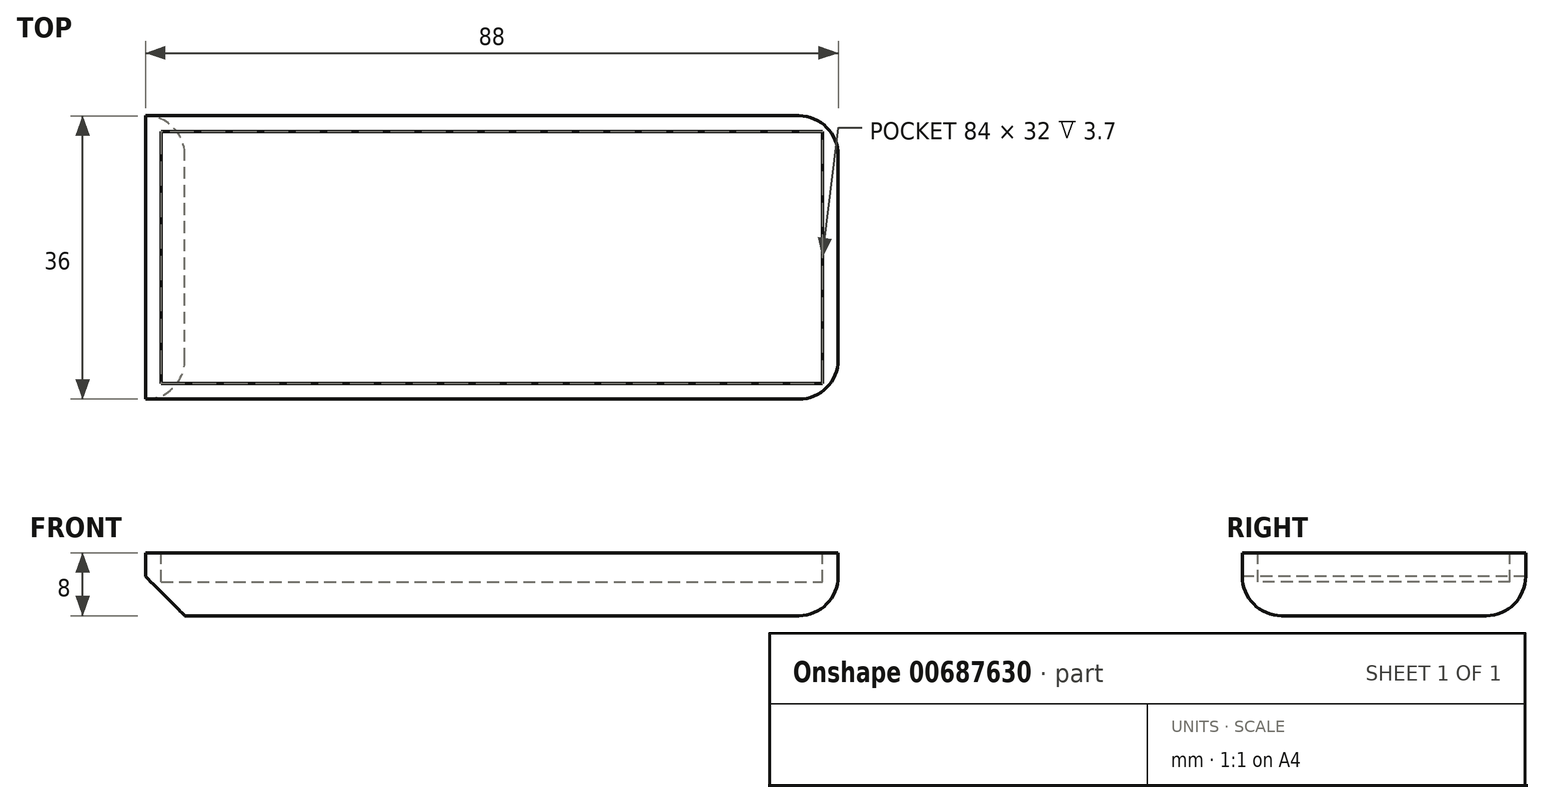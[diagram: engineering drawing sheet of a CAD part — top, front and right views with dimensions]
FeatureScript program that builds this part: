
annotation { "Feature Type Name" : "Feature", "Feature Type Description" : "" }
export const myFeature = defineFeature(function(context is Context, id is Id, definition is map)
    precondition{}
    {
        {
            var Q0;
            Q0=qCreatedBy(makeId("Top.planeOp"),FACE);
            var sketch = newSketch(context, id + "F0", { "sketchPlane" : qUnion([Q0])});
            skLineSegment(sketch, "E0.bottom", {"start": v(-41.02, -2.47) * mm, "end": v(46.98, -2.47) * mm});
            skLineSegment(sketch, "E0.top", {"start": v(-41.02, -38.47) * mm, "end": v(46.98, -38.47) * mm});
            skLineSegment(sketch, "E0.left", {"start": v(-41.02, -2.47) * mm, "end": v(-41.02, -38.47) * mm});
            skLineSegment(sketch, "E0.right", {"start": v(46.98, -2.47) * mm, "end": v(46.98, -38.47) * mm});
            skSolve(sketch);
        }
        {
            var Q0;
            Q0=makeQuery(id+"F0.imprint","IMPRINT",FACE,{"disambiguationData":[TD([[makeQuery(id+"F0.imprint","IMPRINT",EDGE,{"derivedFrom":sQuery(id+"F0.wireOp",EDGE,"E0.bottom")}),-1.0]])]});
            extrude(context, id + "F1", {"entities" : qUnion([Q0]), "depth" : 8 * mm, "offsetDistance" : 25 * mm});
        }
        {
            var Q0;
            Q0=makeQuery(id+"F1.opExtrude","CAP_FACE",FACE,{"disambiguationData":[OSD([sQuery(id+"F0.wireOp",EDGE,"E0.bottom"),sQuery(id+"F0.wireOp",EDGE,"E0.top"),sQuery(id+"F0.wireOp",EDGE,"E0.left"),sQuery(id+"F0.wireOp",EDGE,"E0.right")])],"isStart":false});
            var sketch = newSketch(context, id + "F2", { "sketchPlane" : qUnion([Q0])});
            skLineSegment(sketch, "E1.bottom", {"start": v(-39.02, -4.47) * mm, "end": v(44.98, -4.47) * mm});
            skLineSegment(sketch, "E1.top", {"start": v(-39.02, -36.47) * mm, "end": v(44.98, -36.47) * mm});
            skLineSegment(sketch, "E1.left", {"start": v(-39.02, -4.47) * mm, "end": v(-39.02, -36.47) * mm});
            skLineSegment(sketch, "E1.right", {"start": v(44.98, -4.47) * mm, "end": v(44.98, -36.47) * mm});
            skSolve(sketch);
        }
        {
            var Q0;
            Q0=makeQuery(id+"F2.imprint","IMPRINT",FACE,{"disambiguationData":[TD([[makeQuery(id+"F2.imprint","IMPRINT",EDGE,{"derivedFrom":sQuery(id+"F2.wireOp",EDGE,"E1.bottom")}),-1.0]])]});
            extrude(context, id + "F3", {"entities" : qUnion([Q0]), "operationType" : NewBodyOperationType.REMOVE, "oppositeDirection" : true, "depth" : 3.7 * mm, "offsetDistance" : 25 * mm});
        }
        {
            var Q0;
            Q0=makeQuery(id+"F1.opExtrude","CAP_EDGE",EDGE,{"disambiguationData":[OSD([sQuery(id+"F0.wireOp",EDGE,"E0.left")])],"isStart":true});
            chamfer(context, id + "F4", {"entities" : qUnion([Q0]), "width" : 5 * mm, "tangentPropagation" : true});
        }
        {
            var Q0;
            Q0=makeQuery(id+"F1.opExtrude","CAP_EDGE",EDGE,{"disambiguationData":[OSD([sQuery(id+"F0.wireOp",EDGE,"E0.right")])],"isStart":true});
            var Q1;
            Q1=makeQuery(id+"F1.opExtrude","CAP_EDGE",EDGE,{"disambiguationData":[OSD([sQuery(id+"F0.wireOp",EDGE,"E0.top")])],"isStart":true});
            var Q2;
            Q2=makeQuery(id+"F1.opExtrude","CAP_EDGE",EDGE,{"disambiguationData":[OSD([sQuery(id+"F0.wireOp",EDGE,"E0.bottom")])],"isStart":true});
            var Q3;
            Q3=makeQuery(id+"F1.opExtrude","SWEPT_EDGE",EDGE,{"disambiguationData":[OSD([sQuery(id+"F0.wireOp",EDGE,"E0.top"),sQuery(id+"F0.wireOp",EDGE,"E0.right")])]});
            var Q4;
            Q4=makeQuery(id+"F1.opExtrude","SWEPT_EDGE",EDGE,{"disambiguationData":[OSD([sQuery(id+"F0.wireOp",EDGE,"E0.bottom"),sQuery(id+"F0.wireOp",EDGE,"E0.right")])]});
            fillet(context, id + "F5", {"entities" : qUnion([Q0, Q1, Q2, Q3, Q4]), "radius" : 5 * mm, "tangentPropagation" : true, "allowEdgeOverflow" : false});
        }
    });
